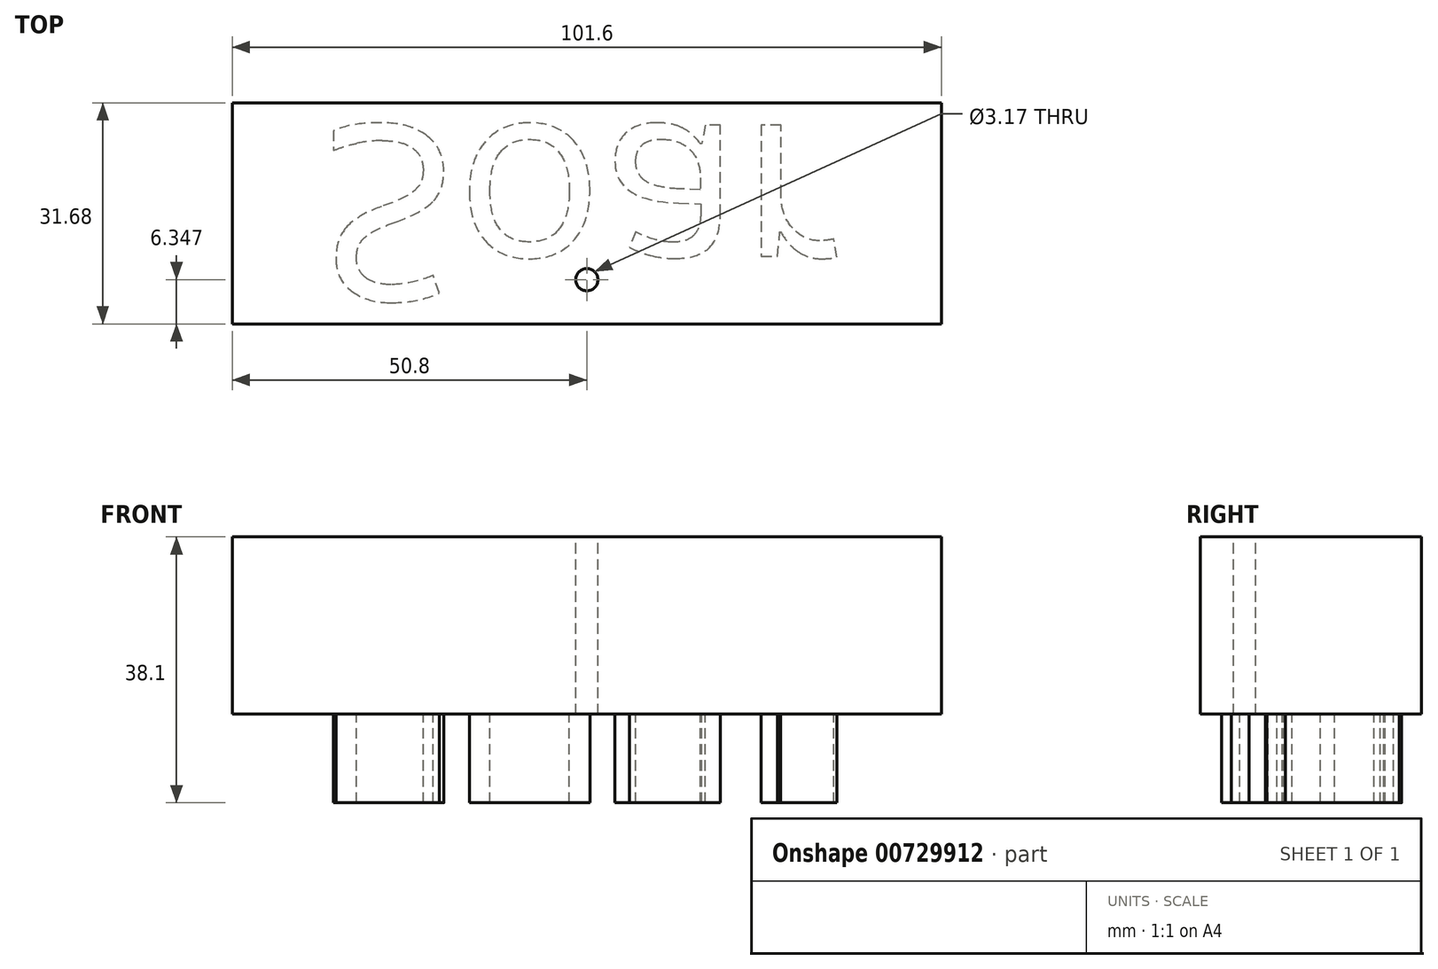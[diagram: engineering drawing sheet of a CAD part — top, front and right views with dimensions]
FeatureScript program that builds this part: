
annotation { "Feature Type Name" : "Feature", "Feature Type Description" : "" }
export const myFeature = defineFeature(function(context is Context, id is Id, definition is map)
    precondition{}
    {
        {
            var Q0;
            Q0=qCreatedBy(makeId("Top.planeOp"),FACE);
            var sketch = newSketch(context, id + "F0", { "sketchPlane" : qUnion([Q0])});
            skLineSegment(sketch, "E0.bottom", {"start": v(50.8, -15.84) * mm, "end": v(-50.8, -15.84) * mm});
            skLineSegment(sketch, "E0.top", {"start": v(50.8, 15.84) * mm, "end": v(-50.8, 15.84) * mm});
            skLineSegment(sketch, "E0.left", {"start": v(50.8, -15.84) * mm, "end": v(50.8, 15.84) * mm});
            skLineSegment(sketch, "E0.right", {"start": v(-50.8, -15.84) * mm, "end": v(-50.8, 15.84) * mm});
            skPoint(sketch, "E0.middle", {"position": v(0, 0) * mm});
            skSolve(sketch);
        }
        {
            var Q0;
            Q0=makeQuery(id+"F0.imprint","IMPRINT",FACE,{"disambiguationData":[TD([[makeQuery(id+"F0.imprint","IMPRINT",EDGE,{"derivedFrom":sQuery(id+"F0.wireOp",EDGE,"E0.bottom")}),-1.0]])]});
            extrude(context, id + "F1", {"entities" : qUnion([Q0]), "depth" : 12.7 * mm, "offsetDistance" : 25.4 * mm});
        }
        {
            var Q0;
            Q0=makeQuery(id+"F1.opExtrude","CAP_FACE",FACE,{"disambiguationData":[OSD([sQuery(id+"F0.wireOp",EDGE,"E0.bottom"),sQuery(id+"F0.wireOp",EDGE,"E0.top"),sQuery(id+"F0.wireOp",EDGE,"E0.left"),sQuery(id+"F0.wireOp",EDGE,"E0.right")])],"isStart":true});
            var sketch = newSketch(context, id + "F2", { "sketchPlane" : qUnion([Q0])});
            skText(sketch, "E1", { "text": "Soar", "fontName": "OpenSans-Regular.ttf"});
            const initialGuessF2  = {"E1": [-0.0381, -0.01265, 1, 0, 0.0253]};
            skSetInitialGuess(sketch, initialGuessF2);
            skSolve(sketch);
        }
        {
            var Q0;
            Q0=makeQuery(id+"F1.opExtrude","CAP_FACE",FACE,{"disambiguationData":[OSD([sQuery(id+"F0.wireOp",EDGE,"E0.bottom"),sQuery(id+"F0.wireOp",EDGE,"E0.top"),sQuery(id+"F0.wireOp",EDGE,"E0.left"),sQuery(id+"F0.wireOp",EDGE,"E0.right")])],"isStart":false});
            extrude(context, id + "F3", {"entities" : qUnion([Q0]), "operationType" : NewBodyOperationType.ADD, "depth" : 12.7 * mm, "offsetDistance" : 25.4 * mm});
        }
        {
            var Q0;
            Q0=makeQuery(id+"F3.opExtrude","CAP_FACE",FACE,{"disambiguationData":[OSD([sQuery(id+"F0.wireOp",EDGE,"E0.bottom"),sQuery(id+"F0.wireOp",EDGE,"E0.top"),sQuery(id+"F0.wireOp",EDGE,"E0.left"),sQuery(id+"F0.wireOp",EDGE,"E0.right")])],"isStart":false});
            var sketch = newSketch(context, id + "F4", { "sketchPlane" : qUnion([Q0])});
            skCircle(sketch, "E2", {"center": v(0, -9.5) * mm, "radius": 1.59 * mm});
            skLineSegment(sketch, "E3", {"start": v(0, -9.5) * mm, "end": v(0, -15.84) * mm});
            skSolve(sketch);
        }
        {
            var Q0;
            Q0 = qSketchRegion(id + "F4", true);
            extrude(context, id + "F5", {"entities" : qUnion([Q0]), "operationType" : NewBodyOperationType.REMOVE, "oppositeDirection" : true, "depth" : 59.18 * mm, "offsetDistance" : 25.4 * mm});
        }
        {
            var Q0;
            Q0 = qSketchRegion(id + "F2", true);
            extrude(context, id + "F6", {"entities" : qUnion([Q0]), "operationType" : NewBodyOperationType.ADD, "depth" : 12.7 * mm, "offsetDistance" : 25.4 * mm});
        }
    });
